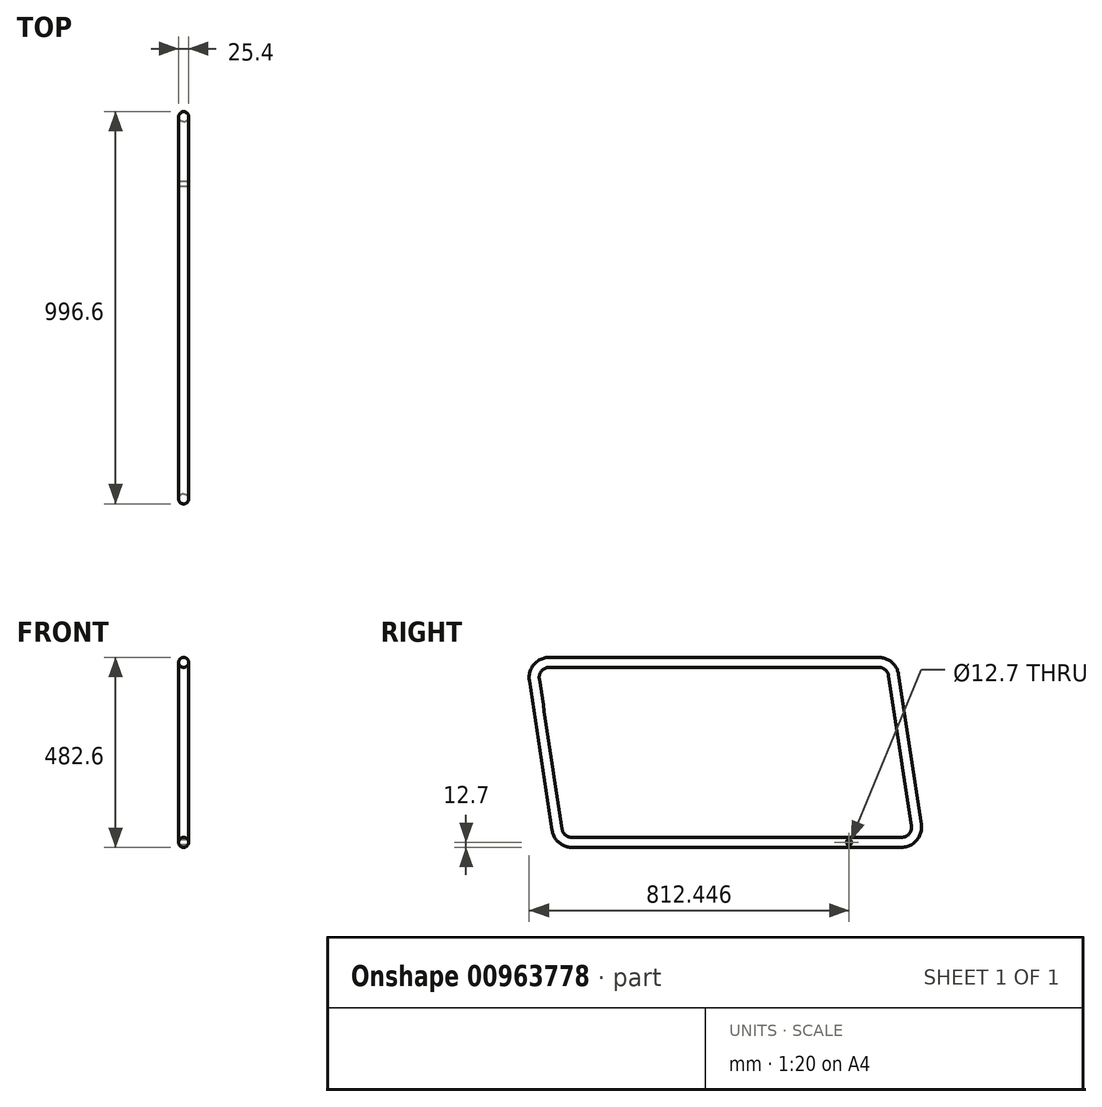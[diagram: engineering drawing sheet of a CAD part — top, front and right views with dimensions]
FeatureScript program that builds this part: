
annotation { "Feature Type Name" : "Feature", "Feature Type Description" : "" }
export const myFeature = defineFeature(function(context is Context, id is Id, definition is map)
    precondition{}
    {
        {
            var Q0;
            Q0=qCreatedBy(makeId("Right.planeOp"),FACE);
            var sketch = newSketch(context, id + "F0", { "sketchPlane" : qUnion([Q0])});
            skLineSegment(sketch, "E0", {"start": v(-379.6, 0) * mm, "end": v(457.74, 0) * mm});
            skLineSegment(sketch, "E1", {"start": v(495.4, 43.8) * mm, "end": v(437.75, 424.8) * mm});
            skLineSegment(sketch, "E2", {"start": v(400.07, 457.2) * mm, "end": v(-437.26, 457.2) * mm});
            skLineSegment(sketch, "E3", {"start": v(-474.93, 413.4) * mm, "end": v(-417.27, 32.4) * mm});
            skPoint(sketch, "E4.visualSharp", {"position": v(432.84, 457.2) * mm});
            skArc(sketch, "E4.filletArc", {"start": v(437.75, 424.8) * mm, "mid": v(424.92, 447.99) * mm, "end": v(400.07, 457.2) * mm});
            skPoint(sketch, "E5.visualSharp", {"position": v(502.04, 0) * mm});
            skArc(sketch, "E5.filletArc", {"start": v(457.74, 0) * mm, "mid": v(486.62, 13.26) * mm, "end": v(495.4, 43.8) * mm});
            skPoint(sketch, "E6.visualSharp", {"position": v(-412.36, 0) * mm});
            skArc(sketch, "E6.filletArc", {"start": v(-417.27, 32.4) * mm, "mid": v(-404.44, 9.21) * mm, "end": v(-379.6, 0) * mm});
            skPoint(sketch, "E7.visualSharp", {"position": v(-481.56, 457.2) * mm});
            skArc(sketch, "E7.filletArc", {"start": v(-437.26, 457.2) * mm, "mid": v(-466.14, 443.94) * mm, "end": v(-474.93, 413.4) * mm});
            skSolve(sketch);
        }
        {
            var Q0;
            Q0=sQuery(id+"F0.wireOp",VERTEX,"E0.start");
            var Q1;
            Q1=sQuery(id+"F0.wireOp",EDGE,"E0");
            cPlane(context, id + "F1", {"entities" : qUnion([Q0, Q1]), "cplaneType" : CPlaneType.LINE_POINT, "offset" : 25.4 * mm, "width" : 152.4 * mm, "height" : 152.4 * mm});
        }
        {
            var Q0;
            Q0=qCreatedBy(id+"F1.planeOp",FACE);
            var sketch = newSketch(context, id + "F2", { "sketchPlane" : qUnion([Q0])});
            skCircle(sketch, "E8", {"center": v(0, 0) * mm, "radius": 12.7 * mm});
            skSolve(sketch);
        }
        {
            var Q0;
            Q0=makeQuery(id+"F2.imprint","IMPRINT",FACE,{"disambiguationData":[TD([[makeQuery(id+"F2.imprint","IMPRINT",EDGE,{"derivedFrom":sQuery(id+"F2.wireOp",EDGE,"E8")}),1.0]])]});
            var Q1;
            Q1 = qConstructionFilter(qBodyType(qCreatedBy(id + "F0" ,EDGE), BodyType.WIRE), ConstructionObject.NO);
            sweep(context, id + "F3", {"profiles" : qUnion([Q0]), "path" : qUnion([Q1])});
        }
        {
            var Q0;
            Q0=qCreatedBy(makeId("Right.planeOp"),FACE);
            var sketch = newSketch(context, id + "F4", { "sketchPlane" : qUnion([Q0])});
            skCircle(sketch, "E9", {"center": v(324.39, 0) * mm, "radius": 6.35 * mm});
            skSolve(sketch);
        }
        {
            var Q0;
            Q0 = qSketchRegion(id + "F4", true);
            var Q1;
            Q1=sQuery(id+"F4.wireOp",EDGE,"E9");
            extrude(context, id + "F5", {"entities" : qUnion([Q0]), "operationType" : NewBodyOperationType.REMOVE, "surfaceEntities" : qUnion([Q1]), "endBound" : BoundingType.SYMMETRIC, "depth" : 25.4 * mm, "offsetDistance" : 25.4 * mm});
        }
    });
